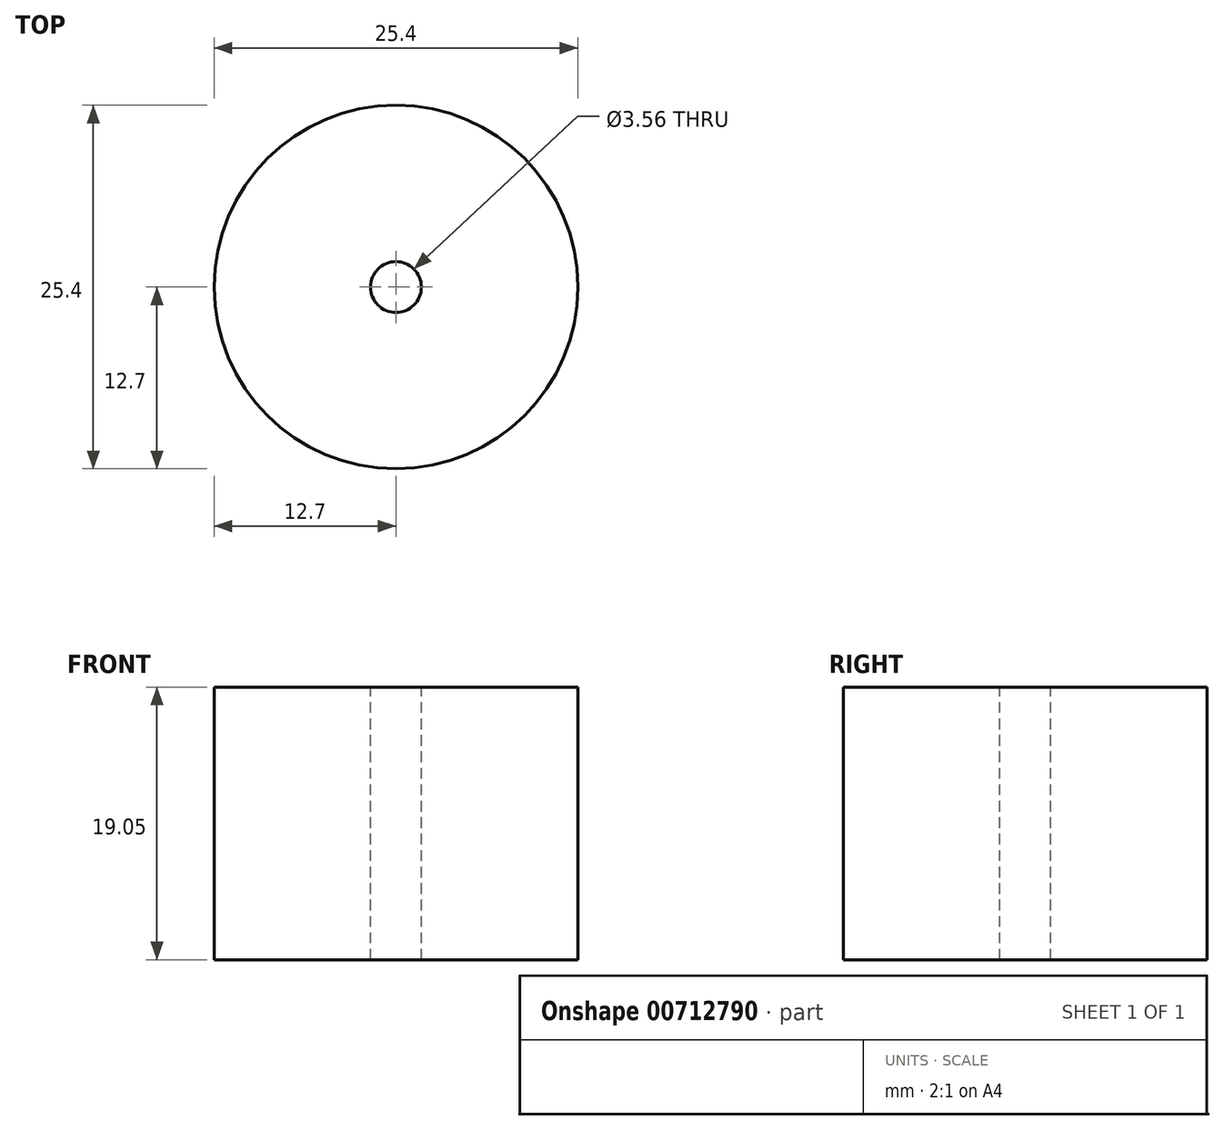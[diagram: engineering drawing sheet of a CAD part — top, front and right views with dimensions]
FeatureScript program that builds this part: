
annotation { "Feature Type Name" : "Feature", "Feature Type Description" : "" }
export const myFeature = defineFeature(function(context is Context, id is Id, definition is map)
    precondition{}
    {
        {
            var Q0;
            Q0=qCreatedBy(makeId("Top.planeOp"),FACE);
            var sketch = newSketch(context, id + "F0", { "sketchPlane" : qUnion([Q0])});
            skLineSegment(sketch, "E0", {"start": v(0, 0) * mm, "end": v(12.7, 0) * mm});
            skLineSegment(sketch, "E1", {"start": v(12.7, 0) * mm, "end": v(-12.7, 0) * mm});
            skLineSegment(sketch, "E2", {"start": v(0, 0) * mm, "end": v(0, 12.7) * mm});
            skLineSegment(sketch, "E3", {"start": v(0, 12.7) * mm, "end": v(0, -12.7) * mm});
            skArc(sketch, "E4", {"start": v(12.7, 0) * mm, "mid": v(0, 12.7) * mm, "end": v(-12.7, 0) * mm});
            skArc(sketch, "E5", {"start": v(-12.7, 0) * mm, "mid": v(0, -12.7) * mm, "end": v(12.7, 0) * mm});
            skSolve(sketch);
        }
        {
            var Q0;
            {var subQ0=sQuery(id+"F0.wireOp",EDGE,"E1");Q0=makeQuery(id+"F0.imprint","IMPRINT",FACE,{"disambiguationData":[TD([[makeQuery(id+"F0.imprint","IMPRINT",EDGE,{"derivedFrom":subQ0}),-1.0]])]});}
            var Q1;
            {var subQ0=sQuery(id+"F0.wireOp",EDGE,"E0");Q1=makeQuery(id+"F0.imprint","IMPRINT",FACE,{"disambiguationData":[TD([[makeQuery(id+"F0.imprint","IMPRINT",EDGE,{"derivedFrom":subQ0}),1.0]])]});}
            var Q2;
            {var subQ0=sQuery(id+"F0.wireOp",EDGE,"E0");Q2=makeQuery(id+"F0.imprint","IMPRINT",FACE,{"disambiguationData":[TD([[makeQuery(id+"F0.imprint","IMPRINT",EDGE,{"derivedFrom":subQ0}),-1.0]])]});}
            var Q3;
            {var subQ0=sQuery(id+"F0.wireOp",EDGE,"E1");Q3=makeQuery(id+"F0.imprint","IMPRINT",FACE,{"disambiguationData":[TD([[makeQuery(id+"F0.imprint","IMPRINT",EDGE,{"derivedFrom":subQ0}),1.0]])]});}
            extrude(context, id + "F1", {"entities" : qUnion([Q0, Q1, Q2, Q3]), "depth" : 19.05 * mm, "offsetDistance" : 25.4 * mm});
        }
        {
            var Q0;
            Q0=makeQuery(id+"F1.opExtrude","CAP_FACE",FACE,{"disambiguationData":[OSD([sQuery(id+"F0.wireOp",EDGE,"E4"),sQuery(id+"F0.wireOp",EDGE,"E5")])],"isStart":false});
            var sketch = newSketch(context, id + "F2", { "sketchPlane" : qUnion([Q0])});
            skLineSegment(sketch, "E6", {"start": v(0, 0) * mm, "end": v(0, 1.78) * mm});
            skLineSegment(sketch, "E7", {"start": v(0, 1.78) * mm, "end": v(0, -1.78) * mm});
            skLineSegment(sketch, "E8", {"start": v(0, 0) * mm, "end": v(1.78, 0) * mm});
            skLineSegment(sketch, "E9", {"start": v(0, 0) * mm, "end": v(-1.78, 0) * mm});
            skArc(sketch, "E10", {"start": v(1.78, 0) * mm, "mid": v(0, 1.78) * mm, "end": v(-1.78, 0) * mm});
            skArc(sketch, "E11", {"start": v(-1.78, 0) * mm, "mid": v(0, -1.78) * mm, "end": v(1.78, 0) * mm});
            skSolve(sketch);
        }
        {
            var Q0;
            {var subQ3=sQuery(id+"F2.wireOp",EDGE,"E9");Q0=makeQuery(id+"F2.imprint","IMPRINT",FACE,{"disambiguationData":[TD([[makeQuery(id+"F2.imprint","IMPRINT",EDGE,{"derivedFrom":subQ3}),-1.0]])]});}
            var Q1;
            {var subQ3=sQuery(id+"F2.wireOp",EDGE,"E8");Q1=makeQuery(id+"F2.imprint","IMPRINT",FACE,{"disambiguationData":[TD([[makeQuery(id+"F2.imprint","IMPRINT",EDGE,{"derivedFrom":subQ3}),1.0]])]});}
            var Q2;
            {var subQ3=sQuery(id+"F2.wireOp",EDGE,"E8");Q2=makeQuery(id+"F2.imprint","IMPRINT",FACE,{"disambiguationData":[TD([[makeQuery(id+"F2.imprint","IMPRINT",EDGE,{"derivedFrom":subQ3}),-1.0]])]});}
            var Q3;
            {var subQ3=sQuery(id+"F2.wireOp",EDGE,"E9");Q3=makeQuery(id+"F2.imprint","IMPRINT",FACE,{"disambiguationData":[TD([[makeQuery(id+"F2.imprint","IMPRINT",EDGE,{"derivedFrom":subQ3}),1.0]])]});}
            extrude(context, id + "F3", {"entities" : qUnion([Q0, Q1, Q2, Q3]), "operationType" : NewBodyOperationType.REMOVE, "oppositeDirection" : true, "depth" : 134.87 * mm, "offsetDistance" : 25.4 * mm});
        }
    });
